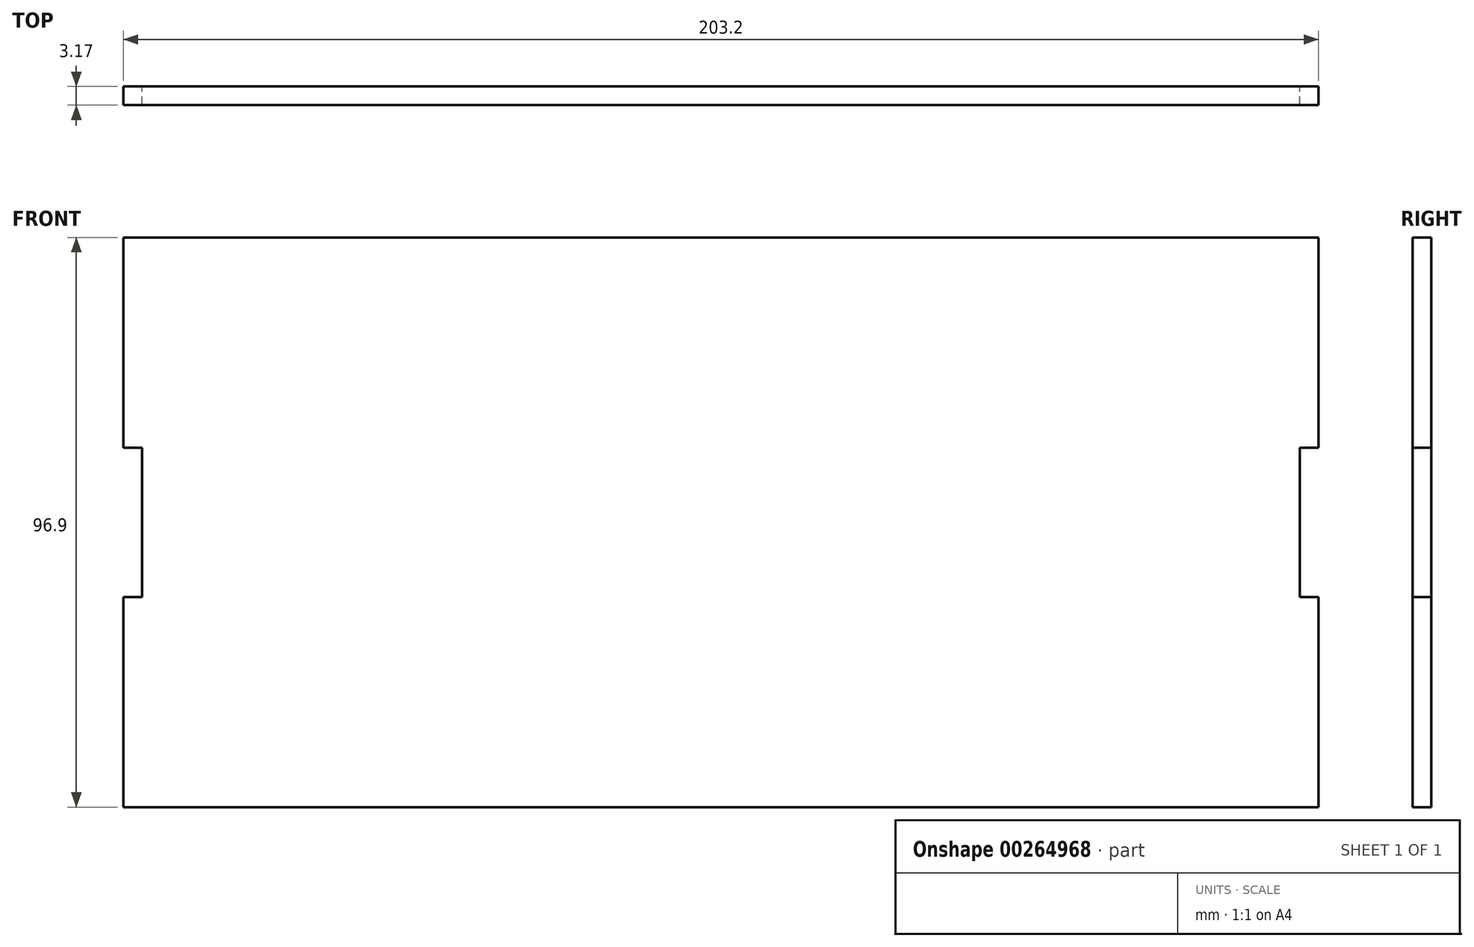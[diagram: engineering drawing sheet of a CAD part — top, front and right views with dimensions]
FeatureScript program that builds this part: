
annotation { "Feature Type Name" : "Feature", "Feature Type Description" : "" }
export const myFeature = defineFeature(function(context is Context, id is Id, definition is map)
    precondition{}
    {
        {
            var Q0;
            Q0=qCreatedBy(makeId("Front.planeOp"),FACE);
            var sketch = newSketch(context, id + "F0", { "sketchPlane" : qUnion([Q0])});
            skLineSegment(sketch, "E0", {"start": v(-101.6, 17.44) * mm, "end": v(-101.6, 53.18) * mm});
            skLineSegment(sketch, "E1", {"start": v(-101.6, -16.6) * mm, "end": v(-101.6, -52.06) * mm});
            skLineSegment(sketch, "E2", {"start": v(-101.6, -43.72) * mm, "end": v(-101.6, -16.6) * mm});
            skLineSegment(sketch, "E3", {"start": v(-104.78, -16.48) * mm, "end": v(-104.78, -16.6) * mm});
            skLineSegment(sketch, "E4", {"start": v(-101.6, 53.18) * mm, "end": v(0, 53.18) * mm});
            skLineSegment(sketch, "E5", {"start": v(0, -43.72) * mm, "end": v(-101.6, -43.72) * mm});
            skPoint(sketch, "E6.start.orphan", {"position": v(0, 0) * mm});
            skLineSegment(sketch, "E7", {"start": v(-104.78, -16.6) * mm, "end": v(-104.78, -16.48) * mm});
            skLineSegment(sketch, "E8", {"start": v(-101.6, -16.48) * mm, "end": v(-101.6, -16.6) * mm});
            skPoint(sketch, "E9.orphan", {"position": v(-104.78, 53.18) * mm});
            skLineSegment(sketch, "E10", {"start": v(-101.6, -16.48) * mm, "end": v(-101.6, -7.97) * mm});
            skPoint(sketch, "E11.orphan", {"position": v(0, 53.18) * mm});
            skPoint(sketch, "E12.MirrorCS.end.orphan", {"position": v(101.6, -43.72) * mm});
            skPoint(sketch, "E12.MirrorCS.start.orphan", {"position": v(0, -43.72) * mm});
            skLineSegment(sketch, "E13.MirrorCS", {"start": v(101.6, 53.18) * mm, "end": v(0, 53.18) * mm});
            skLineSegment(sketch, "E14.MirrorCS", {"start": v(101.6, 17.44) * mm, "end": v(101.6, 53.18) * mm});
            skLineSegment(sketch, "E15.MirrorCS", {"start": v(101.6, -17.6) * mm, "end": v(101.6, -7.97) * mm});
            skLineSegment(sketch, "E16", {"start": v(-101.6, 17.31) * mm, "end": v(-101.6, 17.44) * mm});
            skLineSegment(sketch, "E17", {"start": v(0, -43.72) * mm, "end": v(101.6, -43.72) * mm});
            skLineSegment(sketch, "E18", {"start": v(101.6, -17.6) * mm, "end": v(101.6, -43.72) * mm});
            skLineSegment(sketch, "E19", {"start": v(101.6, 17.44) * mm, "end": v(101.6, 17.31) * mm});
            skLineSegment(sketch, "E20", {"start": v(-101.6, 17.44) * mm, "end": v(-101.6, 17.31) * mm});
            skLineSegment(sketch, "E21.MirrorCS", {"start": v(-98.43, 4.73) * mm, "end": v(-98.43, 17.43) * mm});
            skLineSegment(sketch, "E22.MirrorCS", {"start": v(-98.43, -7.97) * mm, "end": v(-101.6, -7.97) * mm});
            skLineSegment(sketch, "E23.MirrorCS", {"start": v(-98.43, 17.43) * mm, "end": v(-101.6, 17.43) * mm});
            skLineSegment(sketch, "E24.MirrorCS", {"start": v(-98.43, 4.73) * mm, "end": v(-98.43, -7.97) * mm});
            skPoint(sketch, "E25.end.orphan", {"position": v(-101.6, 17.43) * mm});
            skPoint(sketch, "E25.start.orphan", {"position": v(-104.78, 17.43) * mm});
            skPoint(sketch, "E26.end.orphan", {"position": v(-104.78, 4.73) * mm});
            skPoint(sketch, "E27.MirrorCS.end.orphan", {"position": v(-104.78, -7.97) * mm});
            skPoint(sketch, "E28.MirrorCS.end.orphan", {"position": v(-101.6, -7.97) * mm});
            skLineSegment(sketch, "E29.MirrorCS", {"start": v(98.43, 17.43) * mm, "end": v(101.6, 17.43) * mm});
            skLineSegment(sketch, "E30.MirrorCS", {"start": v(98.43, 4.73) * mm, "end": v(98.43, 17.43) * mm});
            skLineSegment(sketch, "E31.MirrorCS", {"start": v(98.43, 4.73) * mm, "end": v(98.43, -7.97) * mm});
            skLineSegment(sketch, "E32.MirrorCS", {"start": v(98.43, -7.97) * mm, "end": v(101.6, -7.97) * mm});
            skSolve(sketch);
        }
        {
            var Q0;
            Q0=makeQuery(id+"F0.imprint","IMPRINT",FACE,{"disambiguationData":[TD([[makeQuery(id+"F0.imprint","IMPRINT",EDGE,{"derivedFrom":sQuery(id+"F0.wireOp",EDGE,"E0")}),-1.0]])]});
            extrude(context, id + "F1", {"entities" : qUnion([Q0]), "depth" : 3.17 * mm});
        }
    });
